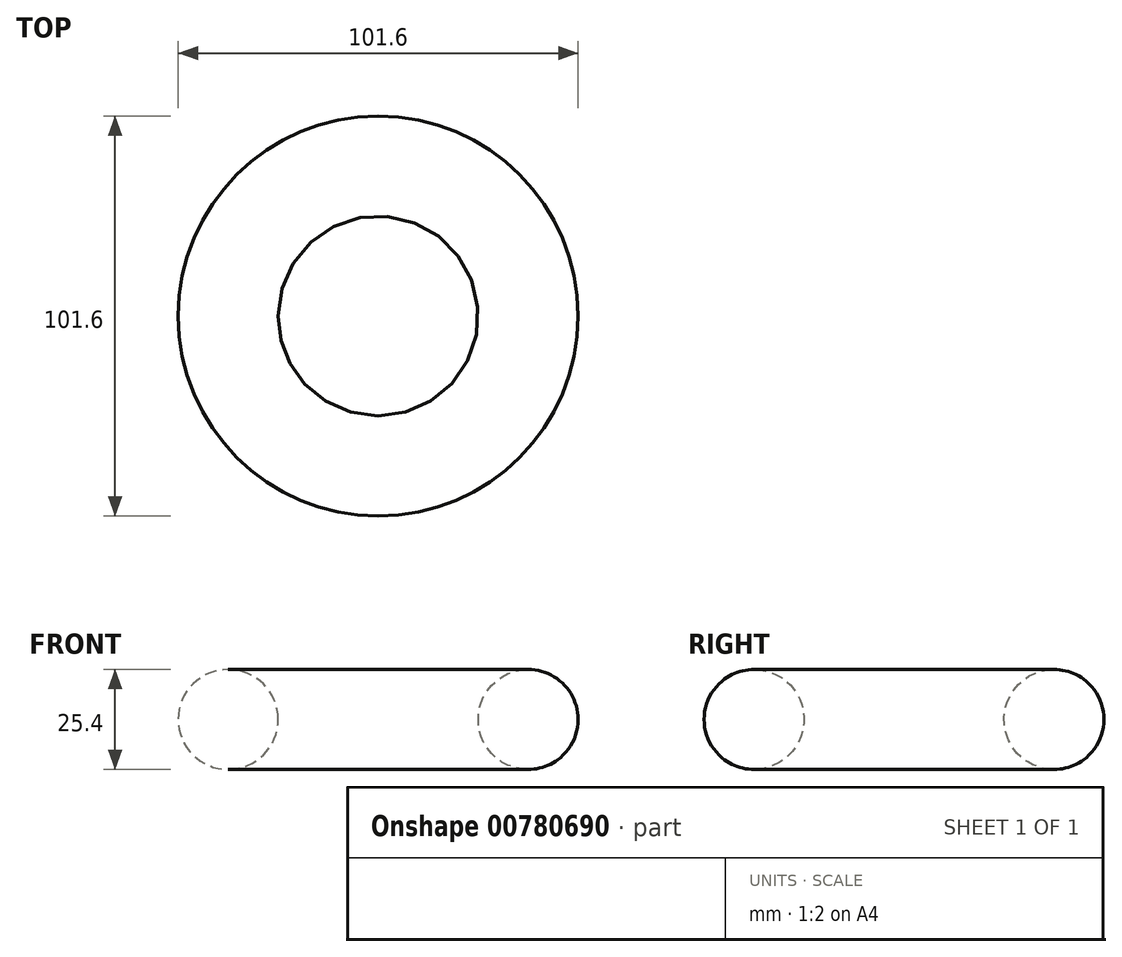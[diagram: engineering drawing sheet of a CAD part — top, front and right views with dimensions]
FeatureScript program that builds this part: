
annotation { "Feature Type Name" : "Feature", "Feature Type Description" : "" }
export const myFeature = defineFeature(function(context is Context, id is Id, definition is map)
    precondition{}
    {
        {
            var Q0;
            Q0=qCreatedBy(makeId("Front.planeOp"),FACE);
            var sketch = newSketch(context, id + "F0", { "sketchPlane" : qUnion([Q0])});
            skCircle(sketch, "E0", {"center": v(38.1, 0) * mm, "radius": 12.7 * mm});
            skLineSegment(sketch, "E1", {"start": v(0, 0) * mm, "end": v(0, 25.35) * mm});
            skSolve(sketch);
        }
        {
            var Q0;
            Q0=makeQuery(id+"F0.imprint","IMPRINT",FACE,{"disambiguationData":[TD([[makeQuery(id+"F0.imprint","IMPRINT",EDGE,{"derivedFrom":sQuery(id+"F0.wireOp",EDGE,"E0")}),1.0]])]});
            var Q1;
            Q1=sQuery(id+"F0.wireOp",EDGE,"E1");
            revolve(context, id + "F1", {"entities" : qUnion([Q0]), "axis" : qUnion([Q1]), "revolveType" : RevolveType.FULL, "surfaceOperationType" : NewSurfaceOperationType.NEW});
        }
    });
